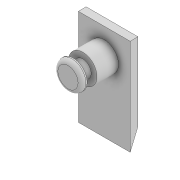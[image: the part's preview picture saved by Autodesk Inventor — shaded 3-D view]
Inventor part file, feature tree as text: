
AUTODESK INVENTOR PART (.ipt)
format: ipt  version: 2022 (Build 260153000, 153)  size: 121,856 bytes
history: native  units: mm
features: extrude x5, sketch x5, fillet x1
ambient origin geometry x8: Origin, YZ Plane, XZ Plane, XY Plane, X Axis, Y Axis, Z Axis, Center Point
bodies: Solid1 (feature_tree)
feature tree (11):
  extrude  "Extrusion1"  Depth=8.3mm TaperAngle=0.0deg
  extrude  "Extrusion2"  Depth=3.7mm TaperAngle=0.0deg
  extrude  "Extrusion3"  Depth=2.0mm TaperAngle=0.0deg
  fillet  "Fillet1"  Radius=1.5mm
  extrude  "Extrusion4"  Depth=20.0mm
  extrude  "Extrusion5"  Depth=10.0mm
  sketch  "Sketch1"  dims[d0=11.0mm d1=8.3mm d2=0.0mm]
  sketch  "Sketch2"  dims[d3=6.5mm d4=3.7mm d5=0.0mm]
  sketch  "Sketch3"  dims[d6=10.8mm d7=2.0mm d8=0.0mm d9=1.5mm]
  sketch  "Sketch4"  dims[d10=20.0mm d11=30.0mm]
  sketch  "Sketch5"  dims[d12=10.0mm d13=10.0mm d14=3.0mm d15=0.0mm d16=6.0mm d17=3.0mm d18=0.0mm]
